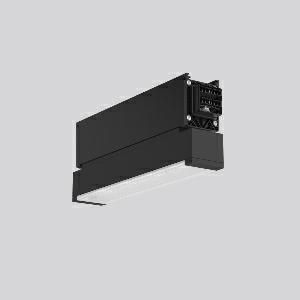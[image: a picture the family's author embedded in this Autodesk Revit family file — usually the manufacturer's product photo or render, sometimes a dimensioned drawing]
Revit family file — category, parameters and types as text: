
# Revit family: linedo_module_rw_9503rw_763_409_00c_3691
name_source: partatom
category: Lighting Fixtures
units: mm (PartAtom-declared; Revit-internal decimal feet)

## family parameters
Cut with Voids When Loaded = No
Host = Face
Light Source = No
Part Type = Normal
Room Calculation Point = No
Round Connector Dimension = Use Diameter
Shared = No

## types (1)
- LINEDO Module RW (1 x LED Modul 763, 340 lm, 6300)
    Apparent Load = 7 VA
    CIE Flux Codes = 36 68 94 98 100
    Color Rendering = 70
    Color Temperature = 6300
    Default Elevation = 1800 mm
    Description = LINEDO, 6,5 W, 340 lm, 763, black, on/off
Continuous line luminaire, L 342 B 58 H 131, CBS, emergency-340 lm, AC-Control
    Height = 131 mm
    Lamp = 1 x LED Modul 763
    Lamp Light Flux = 340 lm
    Lamp count = 1
    Length = 342 mm
    Lifetime = 50000 h
    Luminous efficacy = 52 lm/W
    Manufacturer = RZB
    ModVariant = No
    Model = 9503RW.763.409.00C
    Mounting Place = Ceiling
    Mounting Type = Surface mounted
    Number of Poles = 1
    OnlyDefault = Yes
    Power Factor = 1
    Product Name = LINEDO Module RW
    Product group = Surface mounted continuous line luminaire system
    ProductGroupID = 310
    Protection Class = Protection class I
    Protection Degree = IP 54
    RLX_Detail_Level = 1
    RLX_Emergency_Light_Flux = 340 lm
    RLX_Emergency_Type = 3
    RLX_Emergency_Type_DB = Yes
    RlxData = <blob elided: 34961 chars, md5=7653ea32>
    Socket = socket
    Standby Power = 0 W
    System Light Flux = 340 lm
    System Power = 7 W
    Type Comments = Product without accessories
    Type Image = 9503rf.763.430.00c.jpg
    URL = http://relux.com
    VarID = ---
    Voltage = 230 V
    Voltage Range = 220-240 V
    Weight = 0.00 kg
    Width = 58 mm

## geometry (parser evidence)
native form markers: Blend x4, Sweep x10
no freeform markers — native parametric forms only
